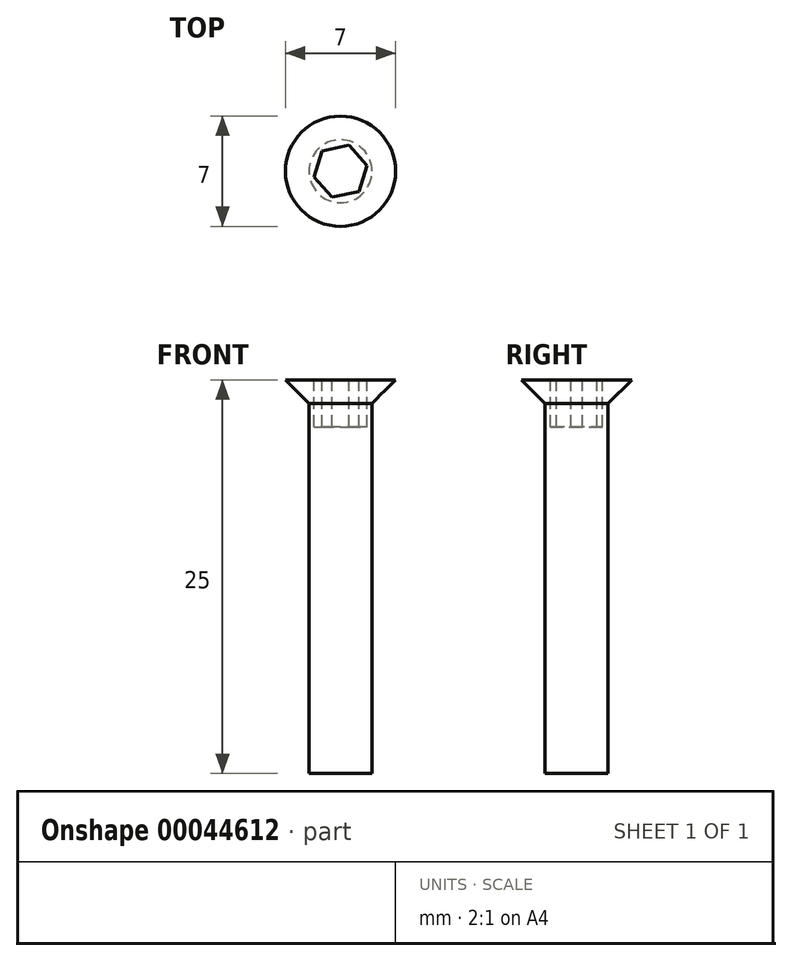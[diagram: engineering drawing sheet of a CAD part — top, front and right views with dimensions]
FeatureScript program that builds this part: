
annotation { "Feature Type Name" : "Feature", "Feature Type Description" : "" }
export const myFeature = defineFeature(function(context is Context, id is Id, definition is map)
    precondition{}
    {
        {
            var Q0;
            Q0=qCreatedBy(makeId("Top.planeOp"),FACE);
            var sketch = newSketch(context, id + "F0", { "sketchPlane" : qUnion([Q0])});
            skCircle(sketch, "E0", {"center": v(0, 0) * mm, "radius": 3.5 * mm});
            skCircle(sketch, "E1", {"center": v(0, 0) * mm, "radius": 2 * mm});
            skCircle(sketch, "E2", {"center": v(0, 0) * mm, "radius": 1.5 * mm, "construction": true});
            skLineSegment(sketch, "E3.0", {"start": v(1.7, 0.37) * mm, "end": v(1.17, -1.28) * mm});
            skLineSegment(sketch, "E3.1", {"start": v(1.17, -1.28) * mm, "end": v(-0.53, -1.65) * mm});
            skLineSegment(sketch, "E3.2", {"start": v(-0.53, -1.65) * mm, "end": v(-1.7, -0.37) * mm});
            skLineSegment(sketch, "E3.3", {"start": v(-1.7, -0.37) * mm, "end": v(-1.17, 1.28) * mm});
            skLineSegment(sketch, "E3.4", {"start": v(-1.17, 1.28) * mm, "end": v(0.53, 1.65) * mm});
            skLineSegment(sketch, "E3.5", {"start": v(0.53, 1.65) * mm, "end": v(1.7, 0.37) * mm});
            skPoint(sketch, "E3.0.midPoint", {"position": v(1.43, -0.46) * mm});
            skSolve(sketch);
        }
        {
            var Q0;
            Q0=makeQuery(id+"F0.imprint","IMPRINT",FACE,{"disambiguationData":[TD([[makeQuery(id+"F0.imprint","IMPRINT",EDGE,{"derivedFrom":sQuery(id+"F0.wireOp",EDGE,"E0")}),1.0]])]});
            var Q1;
            Q1=makeQuery(id+"F0.imprint","IMPRINT",FACE,{"disambiguationData":[TD([[makeQuery(id+"F0.imprint","IMPRINT",EDGE,{"derivedFrom":sQuery(id+"F0.wireOp",EDGE,"E1")}),1.0]])]});
            var Q2;
            Q2=makeQuery(id+"F0.imprint","IMPRINT",FACE,{"disambiguationData":[TD([[makeQuery(id+"F0.imprint","IMPRINT",EDGE,{"derivedFrom":sQuery(id+"F0.wireOp",EDGE,"E3.0")}),-1.0]])]});
            extrude(context, id + "F1", {"entities" : qUnion([Q0, Q1, Q2]), "oppositeDirection" : true, "depth" : 25 * mm, "hasDraft" : true, "draftAngle" : 45 * degree, "draftPullDirection" : true});
        }
        {
            var Q0;
            Q0=makeQuery(id+"F0.imprint","IMPRINT",FACE,{"disambiguationData":[TD([[makeQuery(id+"F0.imprint","IMPRINT",EDGE,{"derivedFrom":sQuery(id+"F0.wireOp",EDGE,"E1")}),1.0]])]});
            var Q1;
            Q1=makeQuery(id+"F0.imprint","IMPRINT",FACE,{"disambiguationData":[TD([[makeQuery(id+"F0.imprint","IMPRINT",EDGE,{"derivedFrom":sQuery(id+"F0.wireOp",EDGE,"E3.0")}),-1.0]])]});
            extrude(context, id + "F2", {"entities" : qUnion([Q0, Q1]), "operationType" : NewBodyOperationType.ADD, "oppositeDirection" : true, "depth" : 25 * mm});
        }
        {
            var Q0;
            Q0=makeQuery(id+"F0.imprint","IMPRINT",FACE,{"disambiguationData":[TD([[makeQuery(id+"F0.imprint","IMPRINT",EDGE,{"derivedFrom":sQuery(id+"F0.wireOp",EDGE,"E3.0")}),-1.0]])]});
            extrude(context, id + "F3", {"entities" : qUnion([Q0]), "operationType" : NewBodyOperationType.REMOVE, "oppositeDirection" : true, "depth" : 3 * mm});
        }
    });
